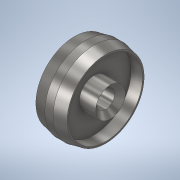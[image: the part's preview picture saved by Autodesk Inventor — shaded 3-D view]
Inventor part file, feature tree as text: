
AUTODESK INVENTOR PART (.ipt)
format: ipt  version: 2020 (Build 240168000, 168)  size: 153,600 bytes
history: native  units: mm
features: revolve x1, sketch x1
ambient origin geometry x8: Origin, YZ Plane, XZ Plane, XY Plane, X Axis, Y Axis, Z Axis, Center Point
bodies: Solid1 (feature_tree)
feature tree (2):
  revolve  "Revolution1"  [1 undecoded]
  sketch  "Sketch1"  dims[d0=50.0mm d1=18.0mm d2=38.0mm d3=11.0mm d4=39.0mm d5=27.0mm d8=10.0mm d9=20.0mm d10=90.0deg d11=34.0mm d12=2.0mm d13=2.0mm d14=18.0mm d15=26.248585mm d16=11.714245mm d17=18.0mm d18=45.0mm]
note: 1 required parameter value undecoded (feature->parameter linkage not recoverable at this tier; creation-order binding heuristic only, values carry confidence <= 0.55)
